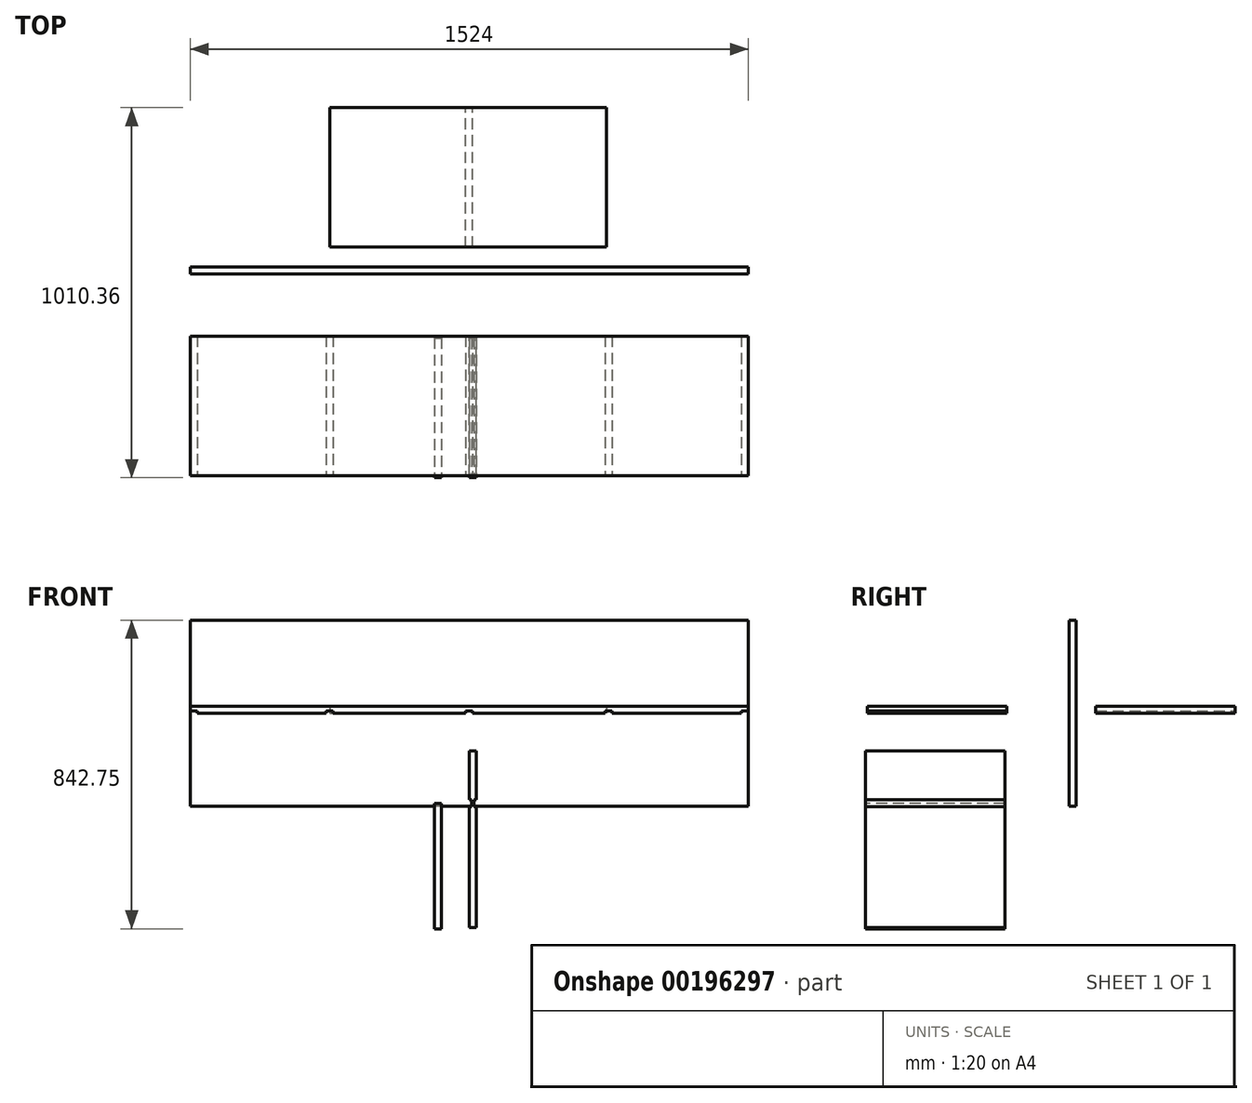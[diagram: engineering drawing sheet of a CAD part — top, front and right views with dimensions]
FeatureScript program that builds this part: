
annotation { "Feature Type Name" : "Feature", "Feature Type Description" : "" }
export const myFeature = defineFeature(function(context is Context, id is Id, definition is map)
    precondition{}
    {
        {
            var Q0;
            Q0=qCreatedBy(makeId("Front.planeOp"),FACE);
            var sketch = newSketch(context, id + "F0", { "sketchPlane" : qUnion([Q0])});
            skLineSegment(sketch, "E0.bottom", {"start": v(762, 254) * mm, "end": v(-762, 254) * mm});
            skLineSegment(sketch, "E0.top", {"start": v(762, -254) * mm, "end": v(-762, -254) * mm});
            skLineSegment(sketch, "E0.left", {"start": v(762, 254) * mm, "end": v(762, -254) * mm});
            skLineSegment(sketch, "E0.right", {"start": v(-762, 254) * mm, "end": v(-762, -254) * mm});
            skPoint(sketch, "E0.middle", {"position": v(0, 0) * mm});
            skSolve(sketch);
        }
        {
            var Q0;
            Q0=makeQuery(id+"F0.imprint","IMPRINT",FACE,{"disambiguationData":[TD([[makeQuery(id+"F0.imprint","IMPRINT",EDGE,{"derivedFrom":sQuery(id+"F0.wireOp",EDGE,"E0.bottom")}),1.0]])]});
            extrude(context, id + "F1", {"entities" : qUnion([Q0]), "depth" : 19.05 * mm});
        }
        {
            var Q0;
            Q0=qCreatedBy(makeId("Top.planeOp"),FACE);
            var sketch = newSketch(context, id + "F2", { "sketchPlane" : qUnion([Q0])});
            skLineSegment(sketch, "E1.bottom", {"start": v(762, -189.2) * mm, "end": v(-762, -189.2) * mm});
            skLineSegment(sketch, "E1.top", {"start": v(762, -570.2) * mm, "end": v(-762, -570.2) * mm});
            skLineSegment(sketch, "E1.left", {"start": v(762, -189.2) * mm, "end": v(762, -570.2) * mm});
            skLineSegment(sketch, "E1.right", {"start": v(-762, -189.2) * mm, "end": v(-762, -570.2) * mm});
            skPoint(sketch, "E1.middle", {"position": v(0, -379.7) * mm});
            skSolve(sketch);
        }
        {
            var Q0;
            Q0=makeQuery(id+"F2.imprint","IMPRINT",FACE,{"disambiguationData":[TD([[makeQuery(id+"F2.imprint","IMPRINT",EDGE,{"derivedFrom":sQuery(id+"F2.wireOp",EDGE,"E1.bottom")}),1.0]])]});
            extrude(context, id + "F3", {"entities" : qUnion([Q0]), "depth" : 19.05 * mm});
        }
        {
            var Q0;
            Q0=qCreatedBy(makeId("Right.planeOp"),FACE);
            var sketch = newSketch(context, id + "F4", { "sketchPlane" : qUnion([Q0])});
            skLineSegment(sketch, "E2.bottom", {"start": v(-575.54, -102.63) * mm, "end": v(-194.54, -102.63) * mm});
            skLineSegment(sketch, "E2.top", {"start": v(-575.54, -585.23) * mm, "end": v(-194.54, -585.23) * mm});
            skLineSegment(sketch, "E2.left", {"start": v(-575.54, -102.63) * mm, "end": v(-575.54, -585.23) * mm});
            skLineSegment(sketch, "E2.right", {"start": v(-194.54, -102.63) * mm, "end": v(-194.54, -585.23) * mm});
            skSolve(sketch);
        }
        {
            var Q0;
            Q0=makeQuery(id+"F4.imprint","IMPRINT",FACE,{"disambiguationData":[TD([[makeQuery(id+"F4.imprint","IMPRINT",EDGE,{"derivedFrom":sQuery(id+"F4.wireOp",EDGE,"E2.bottom")}),-1.0]])]});
            extrude(context, id + "F5", {"entities" : qUnion([Q0]), "depth" : 19.05 * mm});
        }
        {
            var Q0;
            Q0=makeQuery(id+"F3.opExtrude","SWEPT_FACE",FACE,{"disambiguationData":[OSD([sQuery(id+"F2.wireOp",EDGE,"E1.top")])]});
            var sketch = newSketch(context, id + "F6", { "sketchPlane" : qUnion([Q0])});
            skLineSegment(sketch, "E3.bottom", {"start": v(-762, 0) * mm, "end": v(-742.95, 0) * mm});
            skLineSegment(sketch, "E3.top", {"start": v(-762, 6.35) * mm, "end": v(-742.95, 6.35) * mm});
            skLineSegment(sketch, "E3.left", {"start": v(-762, 0) * mm, "end": v(-762, 6.35) * mm});
            skLineSegment(sketch, "E3.right", {"start": v(-742.95, 0) * mm, "end": v(-742.95, 6.35) * mm});
            skLineSegment(sketch, "E4.bottom", {"start": v(762, 0) * mm, "end": v(742.95, 0) * mm});
            skLineSegment(sketch, "E4.top", {"start": v(762, 6.35) * mm, "end": v(742.95, 6.35) * mm});
            skLineSegment(sketch, "E4.left", {"start": v(762, 0) * mm, "end": v(762, 6.35) * mm});
            skLineSegment(sketch, "E4.right", {"start": v(742.95, 0) * mm, "end": v(742.95, 6.35) * mm});
            skLineSegment(sketch, "E5", {"start": v(-381, 0) * mm, "end": v(-381, -45.16) * mm});
            skLineSegment(sketch, "E6", {"start": v(381, 0) * mm, "end": v(381, -18.55) * mm});
            skLineSegment(sketch, "E7.bottom", {"start": v(390.53, 6.35) * mm, "end": v(371.48, 6.35) * mm});
            skLineSegment(sketch, "E7.top", {"start": v(390.53, -6.35) * mm, "end": v(371.48, -6.35) * mm});
            skLineSegment(sketch, "E7.left", {"start": v(390.53, 6.35) * mm, "end": v(390.53, -6.35) * mm});
            skLineSegment(sketch, "E7.right", {"start": v(371.48, 6.35) * mm, "end": v(371.48, -6.35) * mm});
            skPoint(sketch, "E7.middle", {"position": v(381, 0) * mm});
            skLineSegment(sketch, "E8.bottom", {"start": v(-371.48, 6.35) * mm, "end": v(-390.53, 6.35) * mm});
            skLineSegment(sketch, "E8.top", {"start": v(-371.48, -6.35) * mm, "end": v(-390.53, -6.35) * mm});
            skLineSegment(sketch, "E8.left", {"start": v(-371.48, 6.35) * mm, "end": v(-371.48, -6.35) * mm});
            skLineSegment(sketch, "E8.right", {"start": v(-390.53, 6.35) * mm, "end": v(-390.53, -6.35) * mm});
            skPoint(sketch, "E8.middle", {"position": v(-381, 0) * mm});
            skLineSegment(sketch, "E9.bottom", {"start": v(9.53, 6.35) * mm, "end": v(-9.52, 6.35) * mm});
            skLineSegment(sketch, "E9.top", {"start": v(9.53, -6.35) * mm, "end": v(-9.52, -6.35) * mm});
            skLineSegment(sketch, "E9.left", {"start": v(9.53, 6.35) * mm, "end": v(9.53, -6.35) * mm});
            skLineSegment(sketch, "E9.right", {"start": v(-9.52, 6.35) * mm, "end": v(-9.52, -6.35) * mm});
            skPoint(sketch, "E9.middle", {"position": v(0, 0) * mm});
            skSolve(sketch);
        }
        {
            var Q0;
            Q0=makeQuery(id+"F6.imprint","IMPRINT",FACE,{"disambiguationData":[TD([[makeQuery(id+"F6.imprint","IMPRINT",EDGE,{"derivedFrom":sQuery(id+"F6.wireOp",EDGE,"E3.bottom")}),-1.0]])]});
            var Q1;
            {var subQ5=sQuery(id+"F6.wireOp",EDGE,"E8.bottom");Q1=makeQuery(id+"F6.imprint","IMPRINT",FACE,{"disambiguationData":[TD([[makeQuery(id+"F6.imprint","IMPRINT",EDGE,{"derivedFrom":subQ5}),1.0]])]});}
            var Q2;
            {var subQ0=sQuery(id+"F6.wireOp",EDGE,"E9.bottom");Q2=makeQuery(id+"F6.imprint","IMPRINT",FACE,{"disambiguationData":[TD([[makeQuery(id+"F6.imprint","IMPRINT",EDGE,{"derivedFrom":subQ0}),1.0]])]});}
            var Q3;
            {var subQ5=sQuery(id+"F6.wireOp",EDGE,"E7.bottom");Q3=makeQuery(id+"F6.imprint","IMPRINT",FACE,{"disambiguationData":[TD([[makeQuery(id+"F6.imprint","IMPRINT",EDGE,{"derivedFrom":subQ5}),1.0]])]});}
            var Q4;
            Q4=makeQuery(id+"F6.imprint","IMPRINT",FACE,{"disambiguationData":[TD([[makeQuery(id+"F6.imprint","IMPRINT",EDGE,{"derivedFrom":sQuery(id+"F6.wireOp",EDGE,"E4.bottom")}),-1.0]])]});
            extrude(context, id + "F7", {"entities" : qUnion([Q0, Q1, Q2, Q3, Q4]), "operationType" : NewBodyOperationType.REMOVE, "oppositeDirection" : true, "depth" : 381 * mm});
        }
        {
            var Q0;
            Q0=makeQuery(id+"F5.opExtrude","SWEPT_FACE",FACE,{"disambiguationData":[OSD([sQuery(id+"F4.wireOp",EDGE,"E2.left")])]});
            var sketch = newSketch(context, id + "F8", { "sketchPlane" : qUnion([Q0])});
            skLineSegment(sketch, "E10", {"start": v(0, -235.98) * mm, "end": v(-20.17, -235.98) * mm});
            skLineSegment(sketch, "E11.bottom", {"start": v(0, -235.98) * mm, "end": v(6.35, -235.98) * mm});
            skLineSegment(sketch, "E11.top", {"start": v(0, -255.03) * mm, "end": v(6.35, -255.03) * mm});
            skLineSegment(sketch, "E11.left", {"start": v(0, -235.98) * mm, "end": v(0, -255.03) * mm});
            skLineSegment(sketch, "E11.right", {"start": v(6.35, -235.98) * mm, "end": v(6.35, -255.03) * mm});
            skLineSegment(sketch, "E12.bottom", {"start": v(19.05, -235.98) * mm, "end": v(12.7, -235.98) * mm});
            skLineSegment(sketch, "E12.top", {"start": v(19.05, -255.03) * mm, "end": v(12.7, -255.03) * mm});
            skLineSegment(sketch, "E12.left", {"start": v(19.05, -235.98) * mm, "end": v(19.05, -255.03) * mm});
            skLineSegment(sketch, "E12.right", {"start": v(12.7, -235.98) * mm, "end": v(12.7, -255.03) * mm});
            skSolve(sketch);
        }
        {
            var Q0;
            Q0=makeQuery(id+"F8.imprint","IMPRINT",FACE,{"disambiguationData":[TD([[makeQuery(id+"F8.imprint","IMPRINT",EDGE,{"derivedFrom":sQuery(id+"F8.wireOp",EDGE,"E12.bottom")}),1.0]])]});
            var Q1;
            Q1=makeQuery(id+"F8.imprint","IMPRINT",FACE,{"disambiguationData":[TD([[makeQuery(id+"F8.imprint","IMPRINT",EDGE,{"derivedFrom":sQuery(id+"F8.wireOp",EDGE,"E11.bottom")}),-1.0]])]});
            extrude(context, id + "F9", {"entities" : qUnion([Q0, Q1]), "operationType" : NewBodyOperationType.REMOVE, "oppositeDirection" : true, "depth" : 381 * mm});
        }
        {
            var Q0;
            Q0=qCreatedBy(makeId("Top.planeOp"),FACE);
            var sketch = newSketch(context, id + "F10", { "sketchPlane" : qUnion([Q0])});
            skLineSegment(sketch, "E13.bottom", {"start": v(-380.91, 53.82) * mm, "end": v(374.74, 53.82) * mm});
            skLineSegment(sketch, "E13.top", {"start": v(-380.91, 434.82) * mm, "end": v(374.74, 434.82) * mm});
            skLineSegment(sketch, "E13.left", {"start": v(-380.91, 53.82) * mm, "end": v(-380.91, 434.82) * mm});
            skLineSegment(sketch, "E13.right", {"start": v(374.74, 53.82) * mm, "end": v(374.74, 434.82) * mm});
            skSolve(sketch);
        }
        {
            var Q0;
            Q0=makeQuery(id+"F10.imprint","IMPRINT",FACE,{"disambiguationData":[TD([[makeQuery(id+"F10.imprint","IMPRINT",EDGE,{"derivedFrom":sQuery(id+"F10.wireOp",EDGE,"E13.bottom")}),1.0]])]});
            extrude(context, id + "F11", {"entities" : qUnion([Q0]), "depth" : 19.05 * mm});
        }
        {
            var Q0;
            Q0=makeQuery(id+"F11.opExtrude","SWEPT_FACE",FACE,{"disambiguationData":[OSD([sQuery(id+"F10.wireOp",EDGE,"E13.top")])]});
            var sketch = newSketch(context, id + "F12", { "sketchPlane" : qUnion([Q0])});
            skLineSegment(sketch, "E14.bottom", {"start": v(9.53, 6.35) * mm, "end": v(-9.53, 6.35) * mm});
            skLineSegment(sketch, "E14.top", {"start": v(9.53, -6.35) * mm, "end": v(-9.53, -6.35) * mm});
            skLineSegment(sketch, "E14.left", {"start": v(9.53, 6.35) * mm, "end": v(9.53, -6.35) * mm});
            skLineSegment(sketch, "E14.right", {"start": v(-9.53, 6.35) * mm, "end": v(-9.53, -6.35) * mm});
            skPoint(sketch, "E14.middle", {"position": v(0, 0) * mm});
            skSolve(sketch);
        }
        {
            var Q0;
            {var subQ0=sQuery(id+"F12.wireOp",EDGE,"E14.bottom");Q0=makeQuery(id+"F12.imprint","IMPRINT",FACE,{"disambiguationData":[TD([[makeQuery(id+"F12.imprint","IMPRINT",EDGE,{"derivedFrom":subQ0}),1.0]])]});}
            extrude(context, id + "F13", {"entities" : qUnion([Q0]), "operationType" : NewBodyOperationType.REMOVE, "oppositeDirection" : true, "depth" : 381 * mm});
        }
        {
            var Q0;
            Q0=qCreatedBy(makeId("Right.planeOp"),FACE);
            var sketch = newSketch(context, id + "F14", { "sketchPlane" : qUnion([Q0])});
            skLineSegment(sketch, "E15.bottom", {"start": v(-194.17, -245.85) * mm, "end": v(-575.17, -245.85) * mm});
            skLineSegment(sketch, "E15.top", {"start": v(-194.17, -588.75) * mm, "end": v(-575.17, -588.75) * mm});
            skLineSegment(sketch, "E15.left", {"start": v(-194.17, -245.85) * mm, "end": v(-194.17, -588.75) * mm});
            skLineSegment(sketch, "E15.right", {"start": v(-575.17, -245.85) * mm, "end": v(-575.17, -588.75) * mm});
            skSolve(sketch);
        }
        {
            var Q0;
            Q0 = qSketchRegion(id + "F14", true);
            extrude(context, id + "F15", {"entities" : qUnion([Q0]), "operationType" : NewBodyOperationType.ADD, "oppositeDirection" : true, "depth" : 95.25 * mm, "hasSecondDirection" : true, "secondDirectionOppositeDirection" : true, "secondDirectionDepth" : 76.2 * mm});
        }
    });
